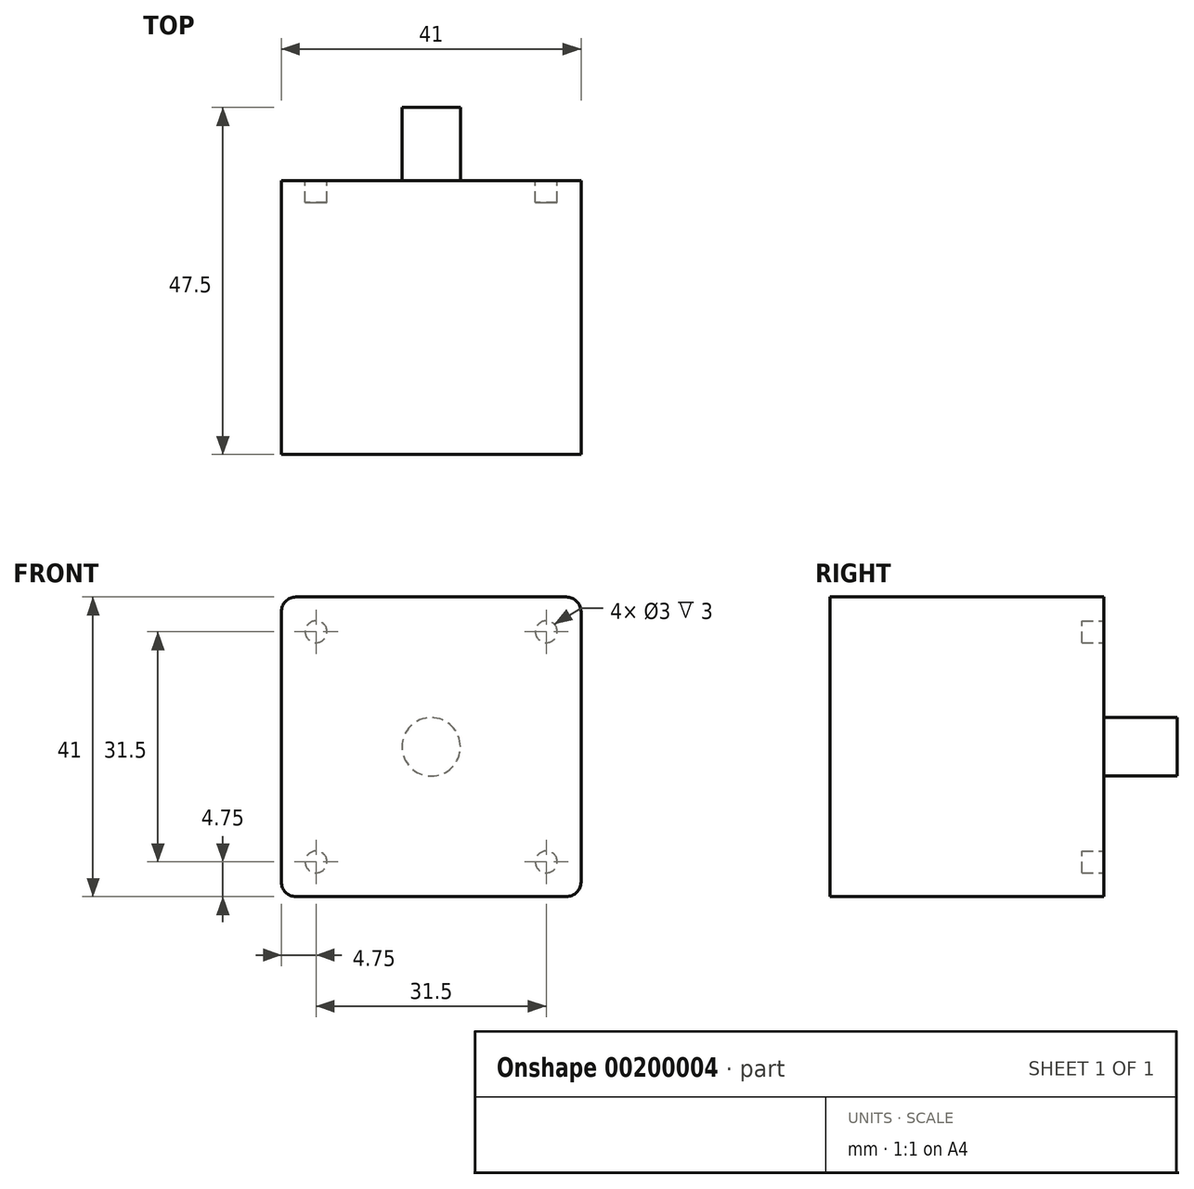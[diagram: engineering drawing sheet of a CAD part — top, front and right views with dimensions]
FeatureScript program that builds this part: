
annotation { "Feature Type Name" : "Feature", "Feature Type Description" : "" }
export const myFeature = defineFeature(function(context is Context, id is Id, definition is map)
    precondition{}
    {
        {
            var Q0;
            Q0=qCreatedBy(makeId("Front.planeOp"),FACE);
            var sketch = newSketch(context, id + "F0", { "sketchPlane" : qUnion([Q0])});
            skLineSegment(sketch, "E0.bottom", {"start": v(0, 0) * mm, "end": v(1000, 0) * mm, "construction": true});
            skLineSegment(sketch, "E0.top", {"start": v(0, 1000) * mm, "end": v(1000, 1000) * mm, "construction": true});
            skLineSegment(sketch, "E0.left", {"start": v(0, 0) * mm, "end": v(0, 1000) * mm, "construction": true});
            skLineSegment(sketch, "E0.right", {"start": v(1000, 0) * mm, "end": v(1000, 1000) * mm, "construction": true});
            skLineSegment(sketch, "E1.bottom", {"start": v(0, 0) * mm, "end": v(100, 0) * mm, "construction": true});
            skLineSegment(sketch, "E1.top", {"start": v(0, 100) * mm, "end": v(100, 100) * mm, "construction": true});
            skLineSegment(sketch, "E1.left", {"start": v(0, 0) * mm, "end": v(0, 100) * mm, "construction": true});
            skLineSegment(sketch, "E1.right", {"start": v(100, 0) * mm, "end": v(100, 100) * mm, "construction": true});
            skSolve(sketch);
        }
        {
            var Q0;
            Q0=qCreatedBy(makeId("Front.planeOp"),FACE);
            var sketch = newSketch(context, id + "F1", { "sketchPlane" : qUnion([Q0])});
            skLineSegment(sketch, "E2.bottom", {"start": v(102, 100) * mm, "end": v(139, 100) * mm});
            skLineSegment(sketch, "E2.top", {"start": v(102, 141) * mm, "end": v(139, 141) * mm});
            skLineSegment(sketch, "E2.left", {"start": v(100, 102) * mm, "end": v(100, 139) * mm});
            skLineSegment(sketch, "E2.right", {"start": v(141, 102) * mm, "end": v(141, 139) * mm});
            skPoint(sketch, "E3", {"position": v(120.5, 120.5) * mm});
            skPoint(sketch, "E3.positionSnap0", {"position": v(100, 120.5) * mm});
            skPoint(sketch, "E3.positionSnap1", {"position": v(120.5, 141) * mm});
            skCircle(sketch, "E4", {"center": v(104.75, 136.25) * mm, "radius": 1.5 * mm});
            skCircle(sketch, "E5", {"center": v(136.25, 136.25) * mm, "radius": 1.5 * mm});
            skCircle(sketch, "E6", {"center": v(136.25, 104.75) * mm, "radius": 1.5 * mm});
            skCircle(sketch, "E7", {"center": v(104.75, 104.75) * mm, "radius": 1.5 * mm});
            skPoint(sketch, "E8", {"position": v(103.25, 136.25) * mm});
            skPoint(sketch, "E9", {"position": v(137.75, 136.25) * mm});
            skLineSegment(sketch, "E10", {"start": v(104.75, 150.28) * mm, "end": v(136.25, 150.28) * mm, "construction": true});
            skPoint(sketch, "E11", {"position": v(120.5, 150.28) * mm});
            skPoint(sketch, "E12", {"position": v(104.75, 137.75) * mm});
            skPoint(sketch, "E13", {"position": v(136.25, 103.25) * mm});
            skPoint(sketch, "E14", {"position": v(137.75, 104.75) * mm});
            skCircle(sketch, "E15", {"center": v(120.5, 120.5) * mm, "radius": 4 * mm});
            skPoint(sketch, "E16.visualSharp", {"position": v(141, 141) * mm});
            skArc(sketch, "E16.filletArc", {"start": v(141, 139) * mm, "mid": v(140.41, 140.41) * mm, "end": v(139, 141) * mm});
            skPoint(sketch, "E17.visualSharp", {"position": v(100, 141) * mm});
            skArc(sketch, "E17.filletArc", {"start": v(102, 141) * mm, "mid": v(100.59, 140.41) * mm, "end": v(100, 139) * mm});
            skPoint(sketch, "E18.visualSharp", {"position": v(100, 100) * mm});
            skArc(sketch, "E18.filletArc", {"start": v(100, 102) * mm, "mid": v(100.59, 100.59) * mm, "end": v(102, 100) * mm});
            skPoint(sketch, "E19.visualSharp", {"position": v(141, 100) * mm});
            skArc(sketch, "E19.filletArc", {"start": v(139, 100) * mm, "mid": v(140.41, 100.59) * mm, "end": v(141, 102) * mm});
            skSolve(sketch);
        }
        {
            var Q0;
            Q0=makeQuery(id+"F1.imprint","IMPRINT",FACE,{"disambiguationData":[TD([[makeQuery(id+"F1.imprint","IMPRINT",EDGE,{"derivedFrom":sQuery(id+"F1.wireOp",EDGE,"E2.bottom")}),1.0]])]});
            var Q1;
            Q1=makeQuery(id+"F1.imprint","IMPRINT",FACE,{"disambiguationData":[TD([[makeQuery(id+"F1.imprint","IMPRINT",EDGE,{"derivedFrom":sQuery(id+"F1.wireOp",EDGE,"E4")}),1.0]])]});
            var Q2;
            Q2=makeQuery(id+"F1.imprint","IMPRINT",FACE,{"disambiguationData":[TD([[makeQuery(id+"F1.imprint","IMPRINT",EDGE,{"derivedFrom":sQuery(id+"F1.wireOp",EDGE,"E5")}),1.0]])]});
            var Q3;
            Q3=makeQuery(id+"F1.imprint","IMPRINT",FACE,{"disambiguationData":[TD([[makeQuery(id+"F1.imprint","IMPRINT",EDGE,{"derivedFrom":sQuery(id+"F1.wireOp",EDGE,"E15")}),1.0]])]});
            var Q4;
            Q4=makeQuery(id+"F1.imprint","IMPRINT",FACE,{"disambiguationData":[TD([[makeQuery(id+"F1.imprint","IMPRINT",EDGE,{"derivedFrom":sQuery(id+"F1.wireOp",EDGE,"E6")}),1.0]])]});
            var Q5;
            Q5=makeQuery(id+"F1.imprint","IMPRINT",FACE,{"disambiguationData":[TD([[makeQuery(id+"F1.imprint","IMPRINT",EDGE,{"derivedFrom":sQuery(id+"F1.wireOp",EDGE,"E7")}),1.0]])]});
            extrude(context, id + "F2", {"entities" : qUnion([Q0, Q1, Q2, Q3, Q4, Q5]), "depth" : 37.5 * mm});
        }
        {
            var Q0;
            Q0=makeQuery(id+"F1.imprint","IMPRINT",FACE,{"disambiguationData":[TD([[makeQuery(id+"F1.imprint","IMPRINT",EDGE,{"derivedFrom":sQuery(id+"F1.wireOp",EDGE,"E6")}),1.0]])]});
            var Q1;
            Q1=makeQuery(id+"F1.imprint","IMPRINT",FACE,{"disambiguationData":[TD([[makeQuery(id+"F1.imprint","IMPRINT",EDGE,{"derivedFrom":sQuery(id+"F1.wireOp",EDGE,"E7")}),1.0]])]});
            var Q2;
            Q2=makeQuery(id+"F1.imprint","IMPRINT",FACE,{"disambiguationData":[TD([[makeQuery(id+"F1.imprint","IMPRINT",EDGE,{"derivedFrom":sQuery(id+"F1.wireOp",EDGE,"E5")}),1.0]])]});
            var Q3;
            Q3=makeQuery(id+"F1.imprint","IMPRINT",FACE,{"disambiguationData":[TD([[makeQuery(id+"F1.imprint","IMPRINT",EDGE,{"derivedFrom":sQuery(id+"F1.wireOp",EDGE,"E4")}),1.0]])]});
            extrude(context, id + "F3", {"entities" : qUnion([Q0, Q1, Q2, Q3]), "operationType" : NewBodyOperationType.REMOVE, "depth" : 3 * mm});
        }
        {
            var Q0;
            Q0=makeQuery(id+"F1.imprint","IMPRINT",FACE,{"disambiguationData":[TD([[makeQuery(id+"F1.imprint","IMPRINT",EDGE,{"derivedFrom":sQuery(id+"F1.wireOp",EDGE,"E15")}),1.0]])]});
            extrude(context, id + "F4", {"entities" : qUnion([Q0]), "operationType" : NewBodyOperationType.ADD, "oppositeDirection" : true, "depth" : 10 * mm});
        }
    });
